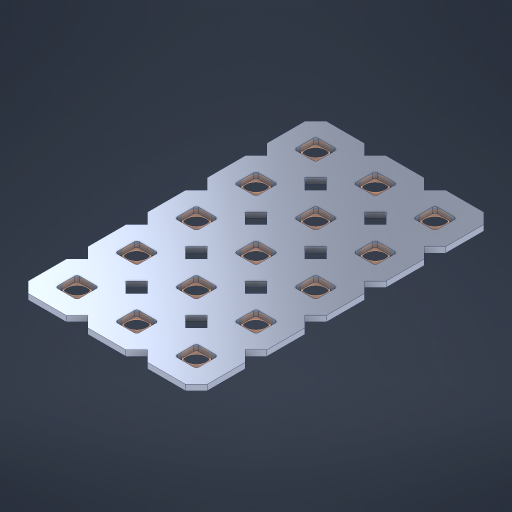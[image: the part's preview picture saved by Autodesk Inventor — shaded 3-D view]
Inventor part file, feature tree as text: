
AUTODESK INVENTOR PART (.ipt)
format: ipt  version: 2023 (Build 270158000, 158)  size: 427,008 bytes
history: native  units: in
note: dims shown in document units (in); Inventor stores cm internally (conversion verified against a paired STEP export)
features: other x16, extrude x14, sketch x2, pattern_linear x1
ambient origin geometry x8: Origin, YZ Plane, XZ Plane, XY Plane, X Axis, Y Axis, Z Axis, Center Point
bodies: Solid1 (feature_tree), Body (feature_tree)
feature tree (33):
  pattern_linear  "Rectangular Pattern1"  Spacing1=0.09in  [1 undecoded]
  sketch  "Sketch1"  dims[d1=0.5in]
  sketch  "Sketch2"  dims[d2=0.182in d3=0.09in d4=0.09in d5=0.09in d6=0.09in d7=0.09in d8=0.09in d9=0.09in d10=0.09in d11=0.02in d13=0.0in d14=0.172in d15=0.0625in d16=0.0in d19=0.5in d22=0.5in]
  other  "Srf1"
  other  "Srf126"
  other  "Srf127"
  other  "Srf128"
  other  "Srf129"
  other  "Srf268"
  other  "Srf269"
  other  "Srf270"
  other  "Srf271"
  other  "Srf272"
  other  "Srf293"
  other  "Srf294"
  other  "Srf295"
  other  "Srf296"
  other  "Srf297"
  other  "Circle"
  extrude  "ExtrusionSrf126"  Depth=0.09in
  extrude  "ExtrusionSrf127"  Depth=0.09in
  extrude  "ExtrusionSrf128"  Depth=0.09in
  extrude  "ExtrusionSrf129"  Depth=0.09in
  extrude  "ExtrusionSrf268"  Depth=0.09in
  extrude  "ExtrusionSrf269"  Depth=0.09in
  extrude  "ExtrusionSrf270"  Depth=0.09in
  extrude  "ExtrusionSrf271"  Depth=0.02in
  extrude  "ExtrusionSrf272"  TaperAngle=0.0deg  [1 undecoded]
  extrude  "ExtrusionSrf293"  Depth=0.5in
  extrude  "ExtrusionSrf294"  Depth=0.5in TaperAngle=0.0deg
  extrude  "ExtrusionSrf295"  Depth=0.5in
  extrude  "ExtrusionSrf296"  Depth=0.5in
  extrude  "ExtrusionSrf297"  [1 undecoded]
note: 3 required parameter values undecoded (feature->parameter linkage not recoverable at this tier; creation-order binding heuristic only, values carry confidence <= 0.55)
